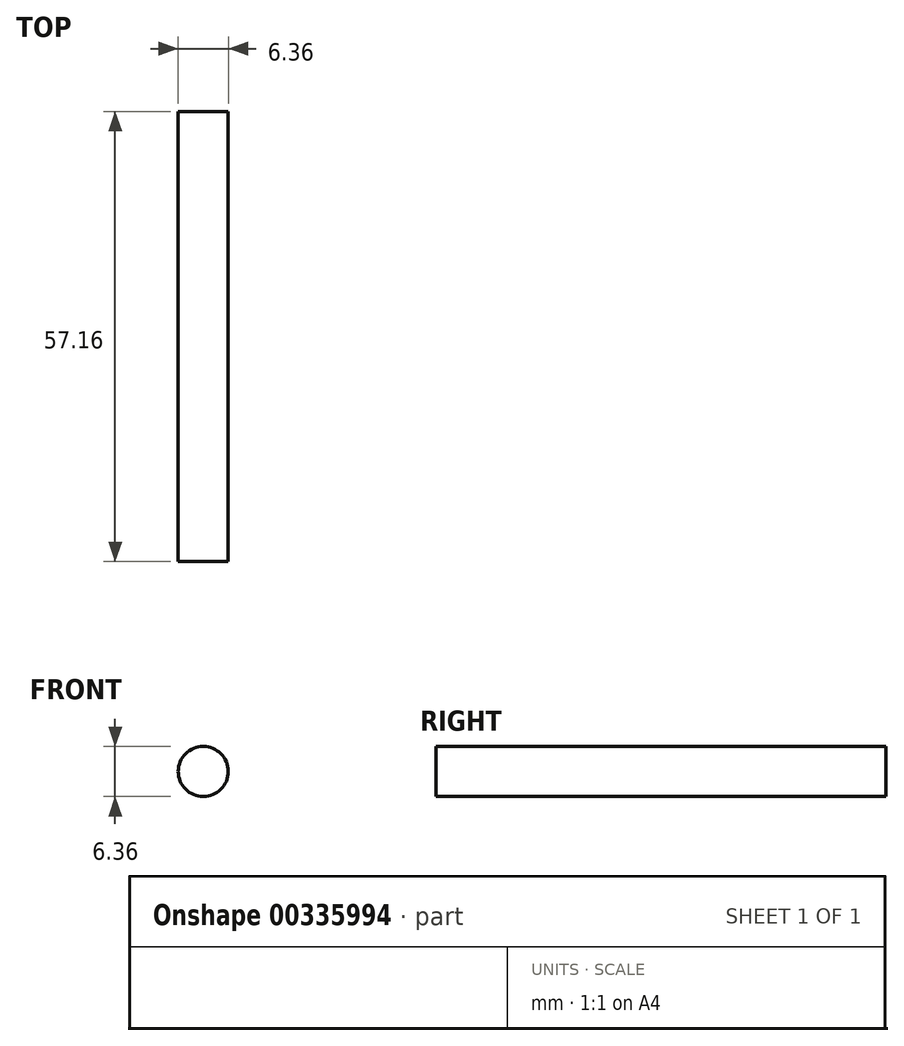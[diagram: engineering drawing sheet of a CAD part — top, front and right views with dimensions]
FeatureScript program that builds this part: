
annotation { "Feature Type Name" : "Feature", "Feature Type Description" : "" }
export const myFeature = defineFeature(function(context is Context, id is Id, definition is map)
    precondition{}
    {
        {
            var Q0;
            Q0=qCreatedBy(makeId("Front.planeOp"),FACE);
            var sketch = newSketch(context, id + "F0", { "sketchPlane" : qUnion([Q0])});
            skCircle(sketch, "E0", {"center": v(0, 0) * mm, "radius": 3.18 * mm});
            skSolve(sketch);
        }
        {
            var Q0;
            Q0=makeQuery(id+"F0.imprint","IMPRINT",FACE,{"disambiguationData":[TD([[makeQuery(id+"F0.imprint","IMPRINT",EDGE,{"derivedFrom":sQuery(id+"F0.wireOp",EDGE,"E0")}),1.0]])]});
            extrude(context, id + "F1", {"entities" : qUnion([Q0]), "endBound" : BoundingType.SYMMETRIC, "depth" : 57.15 * mm});
        }
    });
